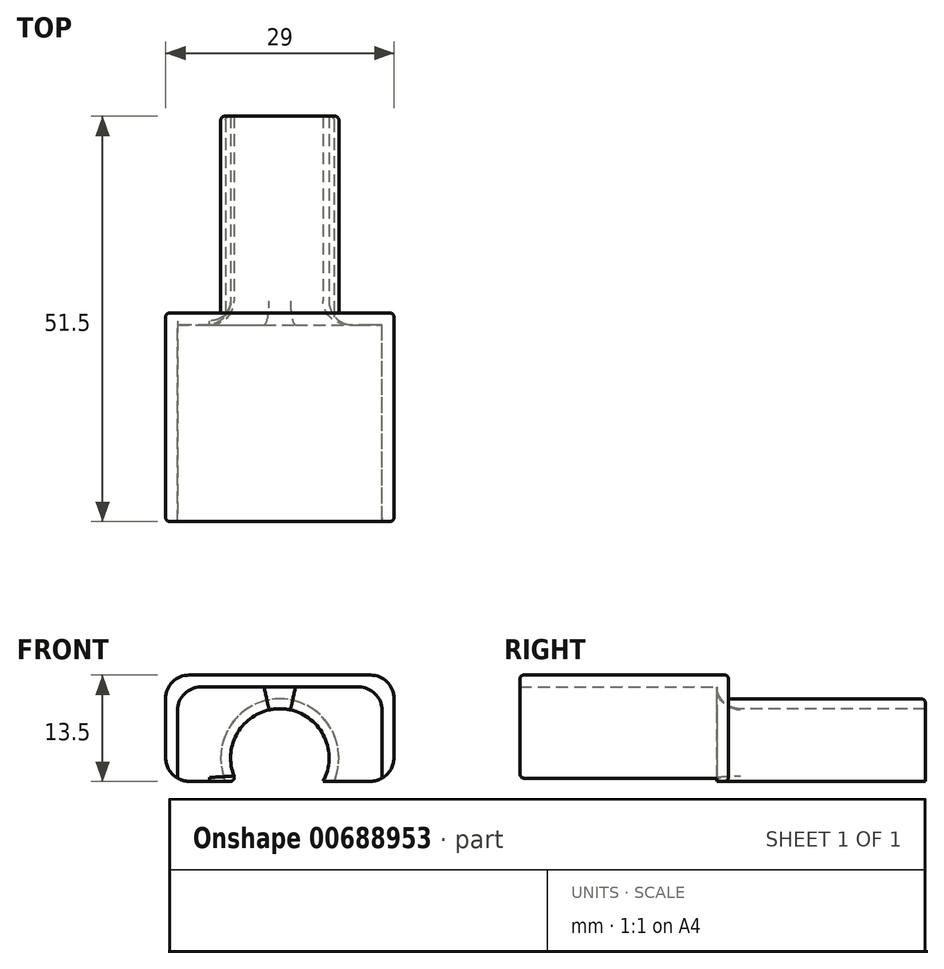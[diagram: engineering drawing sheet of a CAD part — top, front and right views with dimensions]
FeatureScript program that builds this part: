
annotation { "Feature Type Name" : "Feature", "Feature Type Description" : "" }
export const myFeature = defineFeature(function(context is Context, id is Id, definition is map)
    precondition{}
    {
        {
            var Q0;
            Q0=qCreatedBy(makeId("Front.planeOp"),FACE);
            var sketch = newSketch(context, id + "F0", { "sketchPlane" : qUnion([Q0])});
            skLineSegment(sketch, "E0.bottom", {"start": v(0, 0) * mm, "end": v(26, 0) * mm});
            skLineSegment(sketch, "E0.top", {"start": v(0, -12) * mm, "end": v(26, -12) * mm});
            skLineSegment(sketch, "E0.left", {"start": v(0, 0) * mm, "end": v(0, -12) * mm});
            skLineSegment(sketch, "E0.right", {"start": v(26, 0) * mm, "end": v(26, -12) * mm});
            skLineSegment(sketch, "E1.top", {"start": v(0, 1.5) * mm, "end": v(26, 1.5) * mm});
            skLineSegment(sketch, "E1.left", {"start": v(0, 0) * mm, "end": v(0, 1.5) * mm});
            skLineSegment(sketch, "E1.right", {"start": v(26, 0) * mm, "end": v(26, 1.5) * mm});
            skLineSegment(sketch, "E2.bottom", {"start": v(26, 1.5) * mm, "end": v(27.5, 1.5) * mm});
            skLineSegment(sketch, "E2.top", {"start": v(26, -12) * mm, "end": v(27.5, -12) * mm});
            skLineSegment(sketch, "E2.left", {"start": v(26, 1.5) * mm, "end": v(26, -12) * mm});
            skLineSegment(sketch, "E2.right", {"start": v(27.5, 1.5) * mm, "end": v(27.5, -12) * mm});
            skLineSegment(sketch, "E3.bottom", {"start": v(0, 1.5) * mm, "end": v(-1.5, 1.5) * mm});
            skLineSegment(sketch, "E3.top", {"start": v(0, -12) * mm, "end": v(-1.5, -12) * mm});
            skLineSegment(sketch, "E3.left", {"start": v(0, 1.5) * mm, "end": v(0, -12) * mm});
            skLineSegment(sketch, "E3.right", {"start": v(-1.5, 1.5) * mm, "end": v(-1.5, -12) * mm});
            skLineSegment(sketch, "E4.bottom", {"start": v(0, -12) * mm, "end": v(2, -12) * mm});
            skLineSegment(sketch, "E4.top", {"start": v(0, -11) * mm, "end": v(2, -11) * mm});
            skLineSegment(sketch, "E4.left", {"start": v(0, -12) * mm, "end": v(0, -11) * mm});
            skLineSegment(sketch, "E4.right", {"start": v(2, -12) * mm, "end": v(2, -11) * mm});
            skLineSegment(sketch, "E5.bottom", {"start": v(26, -12) * mm, "end": v(24, -12) * mm});
            skLineSegment(sketch, "E5.top", {"start": v(26, -11) * mm, "end": v(24, -11) * mm});
            skLineSegment(sketch, "E5.left", {"start": v(26, -12) * mm, "end": v(26, -11) * mm});
            skLineSegment(sketch, "E5.right", {"start": v(24, -12) * mm, "end": v(24, -11) * mm});
            skLineSegment(sketch, "E6.top", {"start": v(0, -10.5) * mm, "end": v(2, -10.5) * mm});
            skLineSegment(sketch, "E6.left", {"start": v(0, -11) * mm, "end": v(0, -10.5) * mm});
            skLineSegment(sketch, "E6.right", {"start": v(2, -11) * mm, "end": v(2, -10.5) * mm});
            skLineSegment(sketch, "E7.top", {"start": v(26, -10.5) * mm, "end": v(24, -10.5) * mm});
            skLineSegment(sketch, "E7.left", {"start": v(26, -11) * mm, "end": v(26, -10.5) * mm});
            skLineSegment(sketch, "E7.right", {"start": v(24, -11) * mm, "end": v(24, -10.5) * mm});
            skSolve(sketch);
        }
        {
            var Q0;
            Q0=makeQuery(id+"F0.imprint","IMPRINT",FACE,{"disambiguationData":[TD([[makeQuery(id+"F0.imprint","IMPRINT",EDGE,{"derivedFrom":sQuery(id+"F0.wireOp",EDGE,"E4.bottom")}),1.0]])]});
            var Q1;
            Q1=makeQuery(id+"F0.imprint","IMPRINT",FACE,{"disambiguationData":[TD([[makeQuery(id+"F0.imprint","IMPRINT",EDGE,{"derivedFrom":sQuery(id+"F0.wireOp",EDGE,"E5.bottom")}),-1.0]])]});
            var Q2;
            {var subQ0=sQuery(id+"F0.wireOp",EDGE,"E0.bottom");Q2=makeQuery(id+"F0.imprint","IMPRINT",FACE,{"disambiguationData":[TD([[makeQuery(id+"F0.imprint","IMPRINT",EDGE,{"derivedFrom":subQ0}),1.0]])]});}
            var Q3;
            {var subQ3=sQuery(id+"F0.wireOp",EDGE,"E2.bottom");Q3=makeQuery(id+"F0.imprint","IMPRINT",FACE,{"disambiguationData":[TD([[makeQuery(id+"F0.imprint","IMPRINT",EDGE,{"derivedFrom":subQ3}),-1.0]])]});}
            var Q4;
            {var subQ3=sQuery(id+"F0.wireOp",EDGE,"E3.bottom");Q4=makeQuery(id+"F0.imprint","IMPRINT",FACE,{"disambiguationData":[TD([[makeQuery(id+"F0.imprint","IMPRINT",EDGE,{"derivedFrom":subQ3}),1.0]])]});}
            extrude(context, id + "F1", {"entities" : qUnion([Q0, Q1, Q2, Q3, Q4]), "depth" : 25 * mm, "offsetDistance" : 25 * mm});
        }
        {
            var Q0;
            Q0=makeQuery(id+"F1.opExtrude","CAP_FACE",FACE,{"disambiguationData":[OSD([sQuery(id+"F0.wireOp",EDGE,"E0.bottom"),sQuery(id+"F0.wireOp",EDGE,"E1.top"),sQuery(id+"F0.wireOp",EDGE,"E2.bottom"),sQuery(id+"F0.wireOp",EDGE,"E2.top"),sQuery(id+"F0.wireOp",EDGE,"E2.left"),sQuery(id+"F0.wireOp",EDGE,"E2.right"),sQuery(id+"F0.wireOp",EDGE,"E3.bottom"),sQuery(id+"F0.wireOp",EDGE,"E3.top"),sQuery(id+"F0.wireOp",EDGE,"E3.left"),sQuery(id+"F0.wireOp",EDGE,"E3.right"),sQuery(id+"F0.wireOp",EDGE,"E4.bottom"),sQuery(id+"F0.wireOp",EDGE,"E4.right"),sQuery(id+"F0.wireOp",EDGE,"E5.bottom"),sQuery(id+"F0.wireOp",EDGE,"E5.right"),sQuery(id+"F0.wireOp",EDGE,"E4.top"),sQuery(id+"F0.wireOp",EDGE,"E6.left"),sQuery(id+"F0.wireOp",EDGE,"E5.top"),sQuery(id+"F0.wireOp",EDGE,"E7.left")])],"isStart":true});
            var sketch = newSketch(context, id + "F2", { "sketchPlane" : qUnion([Q0])});
            skLineSegment(sketch, "E8.bottom", {"start": v(-27.5, 1.5) * mm, "end": v(1.5, 1.5) * mm});
            skLineSegment(sketch, "E8.top", {"start": v(-27.5, -12) * mm, "end": v(1.5, -12) * mm});
            skLineSegment(sketch, "E8.left", {"start": v(-27.5, 1.5) * mm, "end": v(-27.5, -12) * mm});
            skLineSegment(sketch, "E8.right", {"start": v(1.5, 1.5) * mm, "end": v(1.5, -12) * mm});
            skSolve(sketch);
        }
        {
            var Q0;
            Q0=qSketchRegion(id+"F2",true);
            extrude(context, id + "F3", {"entities" : qUnion([Q0]), "operationType" : NewBodyOperationType.ADD, "depth" : 1.5 * mm, "offsetDistance" : 25 * mm});
        }
        {
            var Q0;
            Q0=makeQuery(id+"F3.opExtrude","CAP_FACE",FACE,{"disambiguationData":[OSD([sQuery(id+"F2.wireOp",EDGE,"E8.bottom"),sQuery(id+"F2.wireOp",EDGE,"E8.top"),sQuery(id+"F2.wireOp",EDGE,"E8.left"),sQuery(id+"F2.wireOp",EDGE,"E8.right")])],"isStart":false});
            var sketch = newSketch(context, id + "F4", { "sketchPlane" : qUnion([Q0])});
            skLineSegment(sketch, "E9", {"start": v(-13, -12) * mm, "end": v(-7.5, -12) * mm, "construction": true});
            skLineSegment(sketch, "E10", {"start": v(-13, -12) * mm, "end": v(-18.5, -12) * mm, "construction": true});
            skArc(sketch, "E11", {"start": v(-7.5, -12) * mm, "mid": v(-13, -2.78) * mm, "end": v(-18.5, -12) * mm});
            skLineSegment(sketch, "E12", {"start": v(-13, -12) * mm, "end": v(-6.11, -12) * mm, "construction": true});
            skLineSegment(sketch, "E13", {"start": v(-13, -12) * mm, "end": v(-19.89, -12) * mm, "construction": true});
            skLineSegment(sketch, "E14", {"start": v(-13, -9.03) * mm, "end": v(-19.89, -12) * mm, "construction": true});
            skLineSegment(sketch, "E15", {"start": v(-13, -9.03) * mm, "end": v(-6.11, -12) * mm, "construction": true});
            skArc(sketch, "E16", {"start": v(-6.11, -12) * mm, "mid": v(-13, -1.53) * mm, "end": v(-19.89, -12) * mm});
            skSolve(sketch);
        }
        {
            var Q0;
            {var subQ0=sQuery(id+"F4.wireOp",EDGE,"E11");Q0=makeQuery(id+"F4.imprint","IMPRINT",FACE,{"disambiguationData":[TD([[makeQuery(id+"F4.imprint","IMPRINT",EDGE,{"derivedFrom":subQ0}),-1.0]])]});}
            extrude(context, id + "F5", {"entities" : qUnion([Q0]), "operationType" : NewBodyOperationType.ADD, "depth" : 25 * mm, "offsetDistance" : 25 * mm});
        }
        {
            var Q0;
            {var subQ0=sQuery(id+"F2.wireOp",EDGE,"E8.top");var subQ1=sQuery(id+"F4.wireOp",EDGE,"E11");Q0=makeQuery(id+"F5.boolean.opBoolean","SPLIT",FACE,{"disambiguationData":[TD([makeQuery(id+"F5.opExtrude","SWEPT_FACE",FACE,{"disambiguationData":[OSD([subQ1])]})])],"derivedFrom":makeQuery(id+"F3.opExtrude","CAP_FACE",FACE,{"disambiguationData":[OSD([sQuery(id+"F2.wireOp",EDGE,"E8.bottom"),subQ0,sQuery(id+"F2.wireOp",EDGE,"E8.left"),sQuery(id+"F2.wireOp",EDGE,"E8.right")])],"isStart":false})});}
            extrude(context, id + "F6", {"entities" : qUnion([Q0]), "operationType" : NewBodyOperationType.REMOVE, "oppositeDirection" : true, "depth" : 25 * mm, "offsetDistance" : 25 * mm});
        }
        {
            var Q0;
            Q0=makeQuery(id+"F1.opExtrude","SWEPT_EDGE",EDGE,{"disambiguationData":[OSD([sQuery(id+"F0.wireOp",EDGE,"E5.left"),sQuery(id+"F0.wireOp",EDGE,"E5.top"),sQuery(id+"F0.wireOp",EDGE,"E7.left")])]});
            var Q1;
            Q1=makeQuery(id+"F1.opExtrude","SWEPT_EDGE",EDGE,{"disambiguationData":[OSD([sQuery(id+"F0.wireOp",EDGE,"E4.left"),sQuery(id+"F0.wireOp",EDGE,"E4.top"),sQuery(id+"F0.wireOp",EDGE,"E6.left")])]});
            var Q2;
            Q2=makeQuery(id+"F1.opExtrude","SWEPT_EDGE",EDGE,{"disambiguationData":[OSD([sQuery(id+"F0.wireOp",EDGE,"E0.bottom"),sQuery(id+"F0.wireOp",EDGE,"E3.left")])]});
            var Q3;
            Q3=makeQuery(id+"F1.opExtrude","SWEPT_EDGE",EDGE,{"disambiguationData":[OSD([sQuery(id+"F0.wireOp",EDGE,"E0.bottom"),sQuery(id+"F0.wireOp",EDGE,"E2.left")])]});
            var Q4;
            Q4=makeQuery(id+"F3.boolean.opBoolean","MERGE",EDGE,{"derivedFrom":[makeQuery(id+"F1.opExtrude","SWEPT_EDGE",EDGE,{"disambiguationData":[OSD([sQuery(id+"F0.wireOp",EDGE,"E3.top"),sQuery(id+"F0.wireOp",EDGE,"E3.right")])]}),makeQuery(id+"F3.opExtrude","SWEPT_EDGE",EDGE,{"disambiguationData":[OSD([sQuery(id+"F2.wireOp",EDGE,"E8.top"),sQuery(id+"F2.wireOp",EDGE,"E8.right")])]})]});
            var Q5;
            Q5=makeQuery(id+"F3.boolean.opBoolean","MERGE",EDGE,{"derivedFrom":[makeQuery(id+"F1.opExtrude","SWEPT_EDGE",EDGE,{"disambiguationData":[OSD([sQuery(id+"F0.wireOp",EDGE,"E3.bottom"),sQuery(id+"F0.wireOp",EDGE,"E3.right")])]}),makeQuery(id+"F3.opExtrude","SWEPT_EDGE",EDGE,{"disambiguationData":[OSD([sQuery(id+"F2.wireOp",EDGE,"E8.bottom"),sQuery(id+"F2.wireOp",EDGE,"E8.right")])]})]});
            var Q6;
            Q6=makeQuery(id+"F3.boolean.opBoolean","MERGE",EDGE,{"derivedFrom":[makeQuery(id+"F1.opExtrude","SWEPT_EDGE",EDGE,{"disambiguationData":[OSD([sQuery(id+"F0.wireOp",EDGE,"E2.bottom"),sQuery(id+"F0.wireOp",EDGE,"E2.right")])]}),makeQuery(id+"F3.opExtrude","SWEPT_EDGE",EDGE,{"disambiguationData":[OSD([sQuery(id+"F2.wireOp",EDGE,"E8.bottom"),sQuery(id+"F2.wireOp",EDGE,"E8.left")])]})]});
            var Q7;
            Q7=makeQuery(id+"F3.boolean.opBoolean","MERGE",EDGE,{"derivedFrom":[makeQuery(id+"F1.opExtrude","SWEPT_EDGE",EDGE,{"disambiguationData":[OSD([sQuery(id+"F0.wireOp",EDGE,"E2.top"),sQuery(id+"F0.wireOp",EDGE,"E2.right")])]}),makeQuery(id+"F3.opExtrude","SWEPT_EDGE",EDGE,{"disambiguationData":[OSD([sQuery(id+"F2.wireOp",EDGE,"E8.top"),sQuery(id+"F2.wireOp",EDGE,"E8.left")])]})]});
            var Q8;
            Q8=makeQuery(id+"F5.opExtrude","CAP_EDGE",EDGE,{"disambiguationData":[OSD([sQuery(id+"F4.wireOp",EDGE,"E16")])],"isStart":true});
            var Q9;
            Q9=makeQuery(id+"F6.boolean.opBoolean","INTERSECT",EDGE,{"derivedFrom":[makeQuery(id+"F3.opExtrude","CAP_FACE",FACE,{"disambiguationData":[OSD([sQuery(id+"F2.wireOp",EDGE,"E8.bottom"),sQuery(id+"F2.wireOp",EDGE,"E8.top"),sQuery(id+"F2.wireOp",EDGE,"E8.left"),sQuery(id+"F2.wireOp",EDGE,"E8.right")])],"isStart":true}),makeQuery(id+"F6.opExtrude","SWEPT_FACE",FACE,{"disambiguationData":[OSD([sQuery(id+"F4.wireOp",EDGE,"E11")])]})]});
            fillet(context, id + "F7", {"entities" : qUnion([Q0, Q1, Q2, Q3, Q4, Q5, Q6, Q7, Q8, Q9]), "radius" : 3 * mm, "tangentPropagation" : true, "allowEdgeOverflow" : false});
        }
        {
            var Q0;
            Q0=makeQuery(id+"F1.opExtrude","SWEPT_EDGE",EDGE,{"disambiguationData":[OSD([sQuery(id+"F0.wireOp",EDGE,"E0.top"),sQuery(id+"F0.wireOp",EDGE,"E5.bottom"),sQuery(id+"F0.wireOp",EDGE,"E5.right")])]});
            var Q1;
            Q1=makeQuery(id+"F1.opExtrude","SWEPT_EDGE",EDGE,{"disambiguationData":[OSD([sQuery(id+"F0.wireOp",EDGE,"E0.top"),sQuery(id+"F0.wireOp",EDGE,"E4.bottom"),sQuery(id+"F0.wireOp",EDGE,"E4.right")])]});
            var Q2;
            {var subQ0=sQuery(id+"F4.wireOp",EDGE,"E11");var subQ1=sQuery(id+"F2.wireOp",EDGE,"E8.top");var subQ2=makeQuery(id+"F4.imprint","INTERSECT",VERTEX,{"disambiguationData":[OD(1.0)],"derivedFrom":[makeQuery(id+"F3.opExtrude","CAP_EDGE",EDGE,{"disambiguationData":[OSD([subQ1])],"isStart":false}),subQ0]});Q2=makeQuery(id+"F6.boolean.opBoolean","MERGE",EDGE,{"derivedFrom":[makeQuery(id+"F5.opExtrude","SWEPT_EDGE",EDGE,{"disambiguationData":[OSD([subQ1,subQ0]),TDD([subQ2])]}),makeQuery(id+"F6.opExtrude","SWEPT_EDGE",EDGE,{"disambiguationData":[OSD([subQ1,subQ0]),TDD([makeQuery(id+"F5.opExtrude","CAP_VERTEX",VERTEX,{"disambiguationData":[OSD([subQ1,subQ0]),TDD([subQ2])],"isStart":true})])]})]});}
            var Q3;
            {var subQ0=sQuery(id+"F4.wireOp",EDGE,"E11");var subQ1=sQuery(id+"F2.wireOp",EDGE,"E8.top");var subQ2=makeQuery(id+"F4.imprint","INTERSECT",VERTEX,{"disambiguationData":[OD(0.0)],"derivedFrom":[makeQuery(id+"F3.opExtrude","CAP_EDGE",EDGE,{"disambiguationData":[OSD([subQ1])],"isStart":false}),subQ0]});Q3=makeQuery(id+"F6.boolean.opBoolean","MERGE",EDGE,{"derivedFrom":[makeQuery(id+"F5.opExtrude","SWEPT_EDGE",EDGE,{"disambiguationData":[OSD([subQ1,subQ0]),TDD([subQ2])]}),makeQuery(id+"F6.opExtrude","SWEPT_EDGE",EDGE,{"disambiguationData":[OSD([subQ1,subQ0]),TDD([makeQuery(id+"F5.opExtrude","CAP_VERTEX",VERTEX,{"disambiguationData":[OSD([subQ1,subQ0]),TDD([subQ2])],"isStart":true})])]})]});}
            var Q4;
            Q4=makeQuery(id+"F5.opExtrude","CAP_EDGE",EDGE,{"disambiguationData":[OSD([sQuery(id+"F4.wireOp",EDGE,"E16")])],"isStart":false});
            var Q5;
            Q5=makeQuery(id+"F1.opExtrude","CAP_EDGE",EDGE,{"disambiguationData":[OSD([sQuery(id+"F0.wireOp",EDGE,"E3.right")])],"isStart":false});
            var Q6;
            Q6=makeQuery(id+"F3.opExtrude","CAP_EDGE",EDGE,{"disambiguationData":[OSD([sQuery(id+"F2.wireOp",EDGE,"E8.left")])],"isStart":false});
            fillet(context, id + "F8", {"entities" : qUnion([Q0, Q1, Q2, Q3, Q4, Q5, Q6]), "radius" : .5 * mm, "tangentPropagation" : true, "allowEdgeOverflow" : false});
        }
    });
